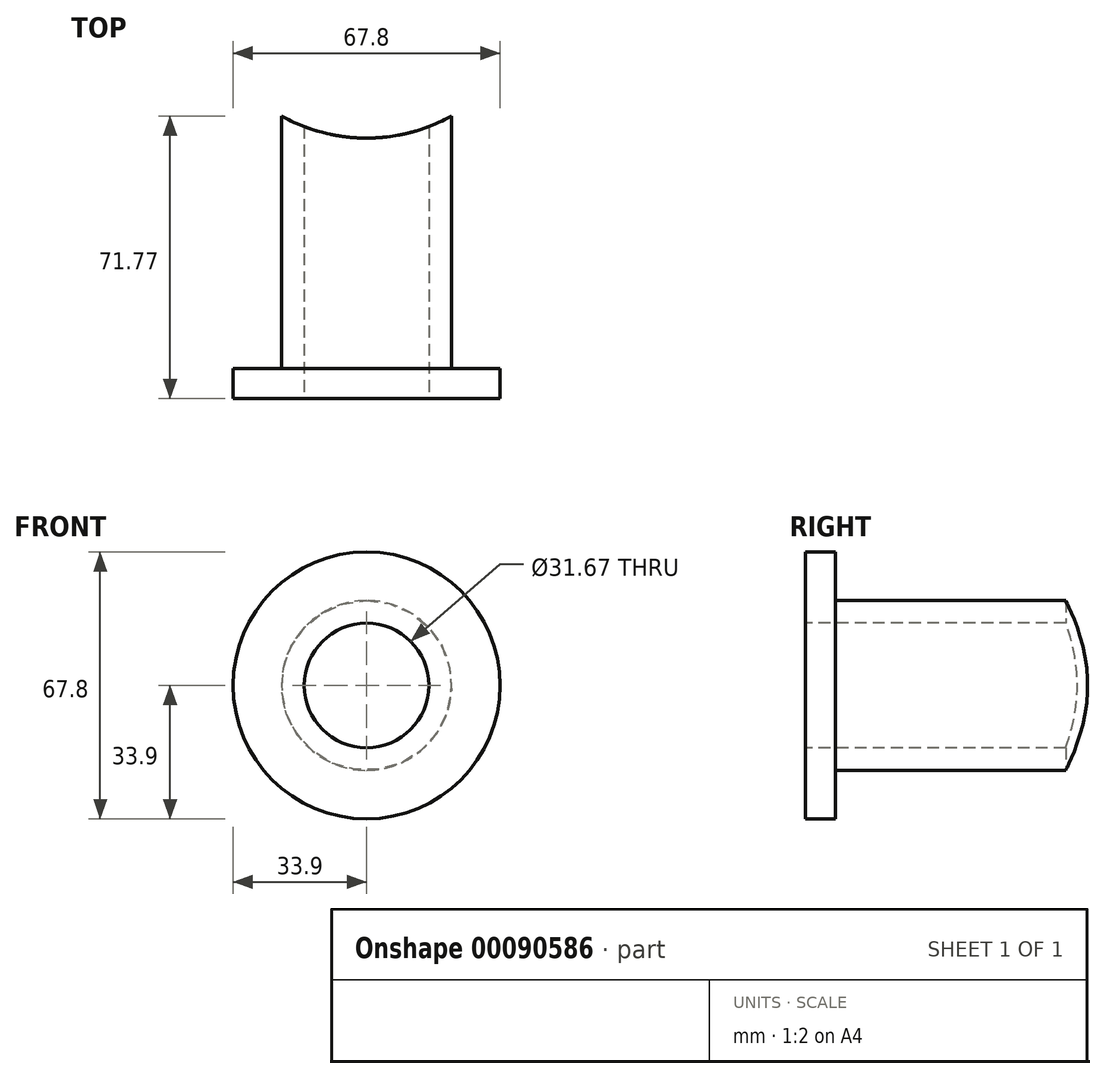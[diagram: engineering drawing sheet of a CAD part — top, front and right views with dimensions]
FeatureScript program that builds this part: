
annotation { "Feature Type Name" : "Feature", "Feature Type Description" : "" }
export const myFeature = defineFeature(function(context is Context, id is Id, definition is map)
    precondition{}
    {
        {
            var Q0;
            Q0=qCreatedBy(makeId("Front.planeOp"),FACE);
            var sketch = newSketch(context, id + "F0", { "sketchPlane" : qUnion([Q0])});
            skCircle(sketch, "E0", {"center": v(0, 0) * mm, "radius": 21.59 * mm});
            skSolve(sketch);
        }
        {
            var Q0;
            Q0=makeQuery(id+"F0.imprint","IMPRINT",FACE,{"disambiguationData":[TD([[makeQuery(id+"F0.imprint","IMPRINT",EDGE,{"derivedFrom":sQuery(id+"F0.wireOp",EDGE,"E0")}),1.0]])]});
            extrude(context, id + "F1", {"entities" : qUnion([Q0]), "depth" : 76.2 * mm});
        }
        {
            var Q0;
            Q0=makeQuery(id+"F1.opExtrude","CAP_FACE",FACE,{"disambiguationData":[OSD([sQuery(id+"F0.wireOp",EDGE,"E0")])],"isStart":false});
            var sketch = newSketch(context, id + "F2", { "sketchPlane" : qUnion([Q0])});
            skCircle(sketch, "E1", {"center": v(0, 0) * mm, "radius": 33.9 * mm});
            skSolve(sketch);
        }
        {
            var Q0;
            Q0=makeQuery(id+"F2.imprint","IMPRINT",FACE,{"disambiguationData":[TD([[makeQuery(id+"F2.imprint","IMPRINT",EDGE,{"derivedFrom":sQuery(id+"F2.wireOp",EDGE,"E1")}),1.0]])]});
            var Q1;
            Q1=makeQuery(id+"F2.imprint","IMPRINT",FACE,{"disambiguationData":[TD([[makeQuery(id+"F2.imprint","IMPRINT",EDGE,{"derivedFrom":makeQuery(id+"F1.opExtrude","CAP_EDGE",EDGE,{"disambiguationData":[OSD([sQuery(id+"F0.wireOp",EDGE,"E0")])],"isStart":false})}),1.0]])]});
            extrude(context, id + "F3", {"entities" : qUnion([Q0, Q1]), "operationType" : NewBodyOperationType.ADD, "depth" : 7.62 * mm});
        }
        {
            var Q0;
            Q0=makeQuery(id+"F3.opExtrude","CAP_FACE",FACE,{"disambiguationData":[OSD([sQuery(id+"F2.wireOp",EDGE,"E1")])],"isStart":false});
            var sketch = newSketch(context, id + "F4", { "sketchPlane" : qUnion([Q0])});
            skCircle(sketch, "E2", {"center": v(0, 0) * mm, "radius": 15.83 * mm});
            skSolve(sketch);
        }
        {
            var Q0;
            Q0=makeQuery(id+"F4.imprint","IMPRINT",FACE,{"disambiguationData":[TD([[makeQuery(id+"F4.imprint","IMPRINT",EDGE,{"derivedFrom":sQuery(id+"F4.wireOp",EDGE,"E2")}),1.0]])]});
            extrude(context, id + "F5", {"entities" : qUnion([Q0]), "operationType" : NewBodyOperationType.REMOVE, "endBound" : BoundingType.THROUGH_ALL, "oppositeDirection" : true, "depth" : 25.4 * mm});
        }
        {
            var Q0;
            Q0=qCreatedBy(makeId("Top.planeOp"),FACE);
            var sketch = newSketch(context, id + "F6", { "sketchPlane" : qUnion([Q0])});
            skCircle(sketch, "E3", {"center": v(0, 26.8) * mm, "radius": 44.45 * mm});
            skSolve(sketch);
        }
        {
            var Q0;
            Q0 = qSketchRegion(id + "F6", true);
            extrude(context, id + "F7", {"entities" : qUnion([Q0]), "operationType" : NewBodyOperationType.REMOVE, "depth" : 25.4 * mm, "hasSecondDirection" : true, "secondDirectionOppositeDirection" : true, "secondDirectionDepth" : 38.48 * mm});
        }
    });
